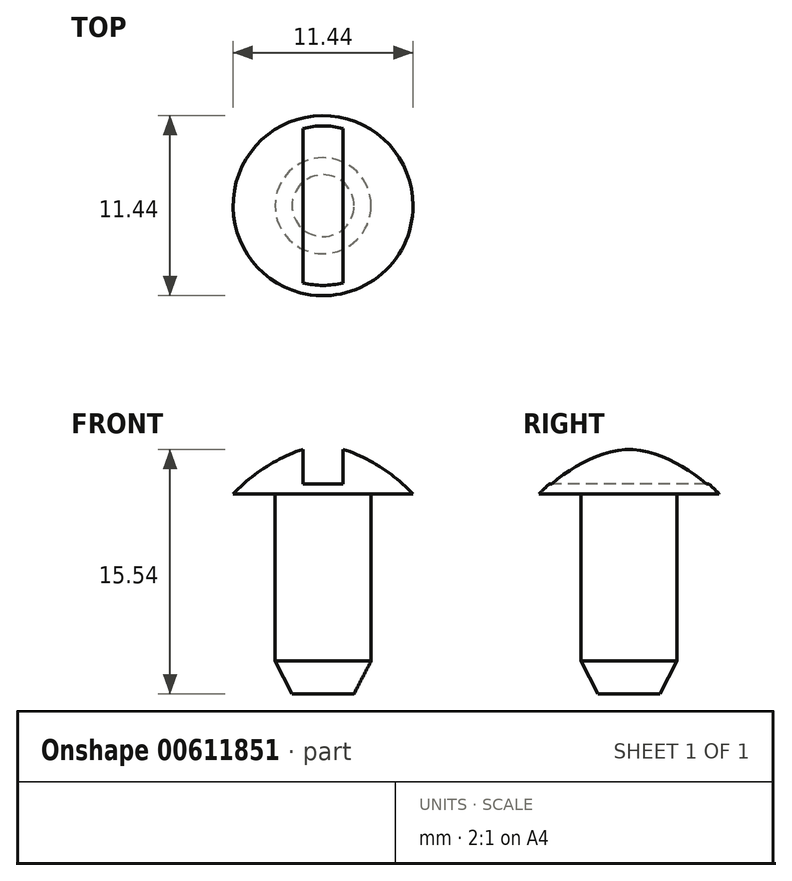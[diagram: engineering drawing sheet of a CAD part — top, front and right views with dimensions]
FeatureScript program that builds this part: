
annotation { "Feature Type Name" : "Feature", "Feature Type Description" : "" }
export const myFeature = defineFeature(function(context is Context, id is Id, definition is map)
    precondition{}
    {
        {
            var Q0;
            Q0=qCreatedBy(makeId("Right.planeOp"),FACE);
            var sketch = newSketch(context, id + "F0", { "sketchPlane" : qUnion([Q0])});
            skLineSegment(sketch, "E0", {"start": v(0, 15.88) * mm, "end": v(0, 0) * mm});
            skLineSegment(sketch, "E1", {"start": v(0, 0) * mm, "end": v(1.97, 0) * mm});
            skLineSegment(sketch, "E2", {"start": v(3.05, 2.09) * mm, "end": v(3.05, 12.7) * mm});
            skLineSegment(sketch, "E3", {"start": v(3.05, 12.7) * mm, "end": v(5.72, 12.7) * mm});
            skArc(sketch, "E4", {"start": v(5.72, 12.7) * mm, "mid": v(3.1, 14.73) * mm, "end": v(0, 15.88) * mm});
            skLineSegment(sketch, "E5", {"start": v(3.05, 2.09) * mm, "end": v(1.97, 0) * mm});
            skSolve(sketch);
        }
        {
            var Q0;
            Q0=makeQuery(id+"F0.imprint","IMPRINT",FACE,{"disambiguationData":[TD([[makeQuery(id+"F0.imprint","IMPRINT",EDGE,{"derivedFrom":sQuery(id+"F0.wireOp",EDGE,"E0")}),1.0]])]});
            var Q1;
            Q1=sQuery(id+"F0.wireOp",EDGE,"E0");
            revolve(context, id + "F1", {"entities" : qUnion([Q0]), "axis" : qUnion([Q1]), "revolveType" : RevolveType.FULL});
        }
        {
            var Q0;
            Q0=qCreatedBy(makeId("Top.planeOp"),FACE);
            cPlane(context, id + "F2", {"entities" : qUnion([Q0]), "cplaneType" : CPlaneType.OFFSET, "offset" : 15.88 * mm, "width" : 152.4 * mm, "height" : 152.4 * mm});
        }
        {
            var Q0;
            Q0=qCreatedBy(id+"F2.planeOp",FACE);
            var sketch = newSketch(context, id + "F3", { "sketchPlane" : qUnion([Q0])});
            skLineSegment(sketch, "E6.bottom", {"start": v(-1.27, 5.08) * mm, "end": v(1.27, 5.08) * mm});
            skLineSegment(sketch, "E6.top", {"start": v(-1.27, -5.08) * mm, "end": v(1.27, -5.08) * mm});
            skLineSegment(sketch, "E6.left", {"start": v(-1.27, 5.08) * mm, "end": v(-1.27, -5.08) * mm});
            skLineSegment(sketch, "E6.right", {"start": v(1.27, 5.08) * mm, "end": v(1.27, -5.08) * mm});
            skPoint(sketch, "E6.middle", {"position": v(0, 0) * mm});
            skSolve(sketch);
        }
        {
            var Q0;
            Q0=makeQuery(id+"F3.imprint","IMPRINT",FACE,{"disambiguationData":[TD([[makeQuery(id+"F3.imprint","IMPRINT",EDGE,{"derivedFrom":sQuery(id+"F3.wireOp",EDGE,"E6.bottom")}),-1.0]])]});
            extrude(context, id + "F4", {"entities" : qUnion([Q0]), "operationType" : NewBodyOperationType.REMOVE, "oppositeDirection" : true, "depth" : 2.54 * mm, "offsetDistance" : 25.4 * mm});
        }
    });
